# Revit family: Hydrant_Wall-Zurn-Z1305-Encased, Non-Freeze
name_source: partatom
category: Plumbing Fixtures
units: mm (PartAtom-declared; Revit-internal decimal feet)

## family parameters
Cut with Voids When Loaded = No
Host = Face
Maintain Annotation Orientation = No
OmniClass Number = 23.65.70.00
OmniClass Title = Terminals for Supplied Liquids and Gases
Part Type = Normal
Room Calculation Point = No
Round Connector Dimension = Use Radius
Shared = No

## types (14) — shared parameters
Assembly Code = D2020100
Box Height = 2.281 "
Box Width = 6.375 "
CW Connection = Yes
CWFU = 1
Cartridge housing = 2.75 "
Default Elevation = 25 "
Description = Wall Hydrant Encased, Non-Freeze
HW Connection = No
Main Material = Bronze - Zurn - Casing
Manufacturer = Zurn Water, LLC
Manufacturer Brand = Zurn
Model = Z1305
Modified Date = 10/10/2025
Product Documentation Link = https://files.zurn.com
Product Page URL = https://www.zurn.com
Product data url = https://www.bimobject.com
URL = www.zurn.com
Vent Connection = No
Waste Connection = No
zero-valued in all types: HWFU, WFU

## per-type parameters (varying)
| type | Approx.wt.Lbs | Female and Male Connector | Female and Male Radius | Type Comments | Wall thicknesss |
| Z1305 - 6" Wall Hydrant w/ 3/4" Female Inlet | 11 " | 0.375 " | 0.525 " | Z1305 - 6 Inch Wall Hydrant with 3/4 Inch Female Inlet | 6 " |
| Z1305 - 6" Wall Hydrant w/ 1" Male Inlet | 11 " | 0.5 " | 0.658 " | Z1305 - 6 Inch Wall Hydrant with 1 Inch Male Inlet | 6 " |
| Z1305 - 8" Wall Hydrant w/ 3/4" Female Inlet | 11 " | 0.375 " | 0.525 " | Z1305 - 8 Inch Wall Hydrant with 3/4 Inch Female Inlet | 8 " |
| Z1305 - 8" Wall Hydrant w/ 1" Male Inlet | 11 " | 0.5 " | 0.658 " | Z1305 - 8 Inch Wall Hydrant with 1 Inch Male Inlet | 8 " |
| Z1305 - 10 Wall Hydrant w/ 3/4 Male Inlet | 13 " | 0.375 " | 0.525 " | Z1305 - 10 Inch Wall Hydrant with 3/4 Inch Female Inlet | 10 " |
| Z1305 - 10 Wall Hydrant w/ 1 Male Inlet | 13 " | 0.5 " | 0.658 " | Z1305 - 10 Inch Wall Hydrant with 1 Inch Male Inlet | 10 " |
| Z1305 - 12" Wall Hydrant w/ 3/4" Female Inlet | 13 " | 0.375 " | 0.525 " | Z1305 - 12 Inch Wall Hydrant with 3/4 Inch Female Inlet | 12 " |
| Z1305 - 12" Wall Hydrant w/ 1" Male Inlet | 13 " | 0.5 " | 0.658 " | Z1305 - 12 Inch Wall Hydrant with 1 Inch Male Inlet | 12 " |
| Z1305 - 14" Wall Hydrant w/ 3/4" Female Inlet | 13 " | 0.375 " | 0.525 " | Z1305 - 14 Inch Wall Hydrant with 3/4 Inch Female Inlet | 14 " |
| Z1305 - 14" Wall Hydrant w/ 1" Male Inlet | 13 " | 0.5 " | 0.658 " | Z1305 - 14 Inch Wall Hydrant with 1 Inch Male Inlet | 14 " |
| Z1305 - 16" Wall Hydrant w/ 3/4" Female Inlet | 15 " | 0.375 " | 0.525 " | Z1305 - 16 Inch Wall Hydrant with 3/4 Inch Female Inlet | 16 " |
| Z1305 - 16" Wall Hydrant w/ 1" Male Inlet | 15 " | 0.5 " | 0.658 " | Z1305 - 16 Inch Wall Hydrant with 1 Inch Male Inlet | 16 " |
| Z1305 - 24" Wall Hydrant w/ 3/4" Female Inlet | 17 " | 0.375 " | 0.525 " | Z1305 - 24 Inch Wall Hydrant with 3/4 Inch Female Inlet | 24 " |
| Z1305 - 24" Wall Hydrant w/ 1" Male Inlet | 17 " | 0.5 " | 0.658 " | Z1305 - 24 Inch Wall Hydrant with 1 Inch Male Inlet | 24 " |

## geometry (parser evidence)
native form markers: Blend x12, Sweep x6
no freeform markers — native parametric forms only
